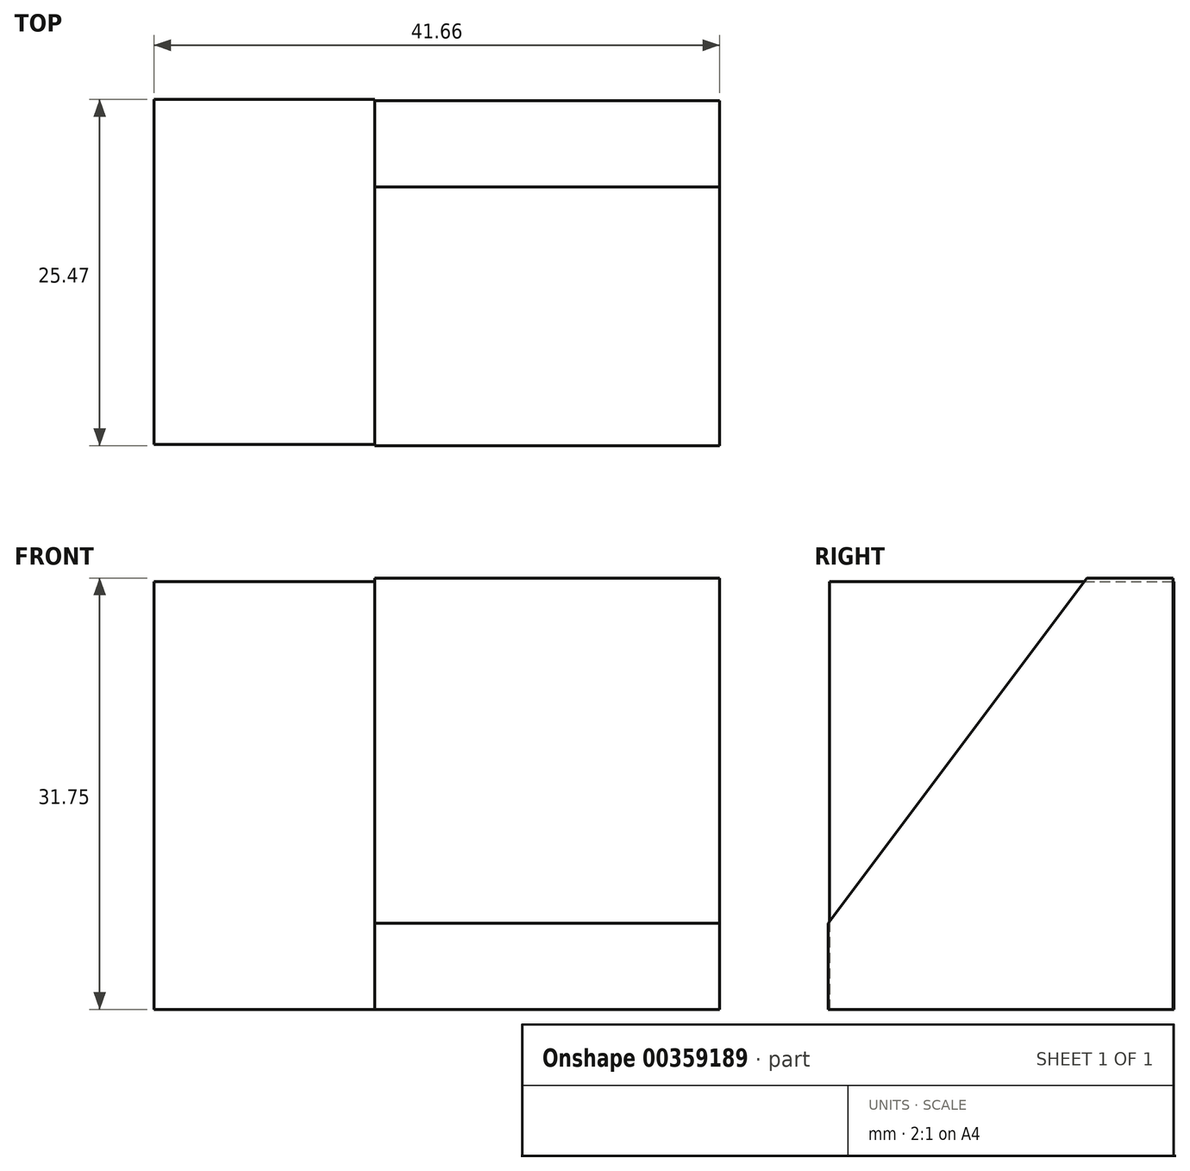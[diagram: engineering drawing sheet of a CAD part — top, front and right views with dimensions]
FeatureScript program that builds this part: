
annotation { "Feature Type Name" : "Feature", "Feature Type Description" : "" }
export const myFeature = defineFeature(function(context is Context, id is Id, definition is map)
    precondition{}
    {
        {
            var Q0;
            Q0=qCreatedBy(makeId("Right.planeOp"),FACE);
            var sketch = newSketch(context, id + "F0", { "sketchPlane" : qUnion([Q0])});
            skLineSegment(sketch, "E0", {"start": v(0, 31.75) * mm, "end": v(6.35, 31.75) * mm});
            skLineSegment(sketch, "E1", {"start": v(6.35, 31.75) * mm, "end": v(6.35, 0) * mm});
            skLineSegment(sketch, "E2", {"start": v(6.35, 0) * mm, "end": v(-19.05, 0) * mm});
            skLineSegment(sketch, "E3", {"start": v(-19.05, 0) * mm, "end": v(-19.05, 6.35) * mm});
            skLineSegment(sketch, "E4", {"start": v(-19.05, 6.35) * mm, "end": v(0, 31.75) * mm});
            skSolve(sketch);
        }
        {
            var Q0;
            Q0 = qSketchRegion(id + "F0", true);
            var Q1;
            Q1=makeQuery(id+"F0.imprint","IMPRINT",FACE,{"disambiguationData":[TD([[makeQuery(id+"F0.imprint","IMPRINT",EDGE,{"derivedFrom":sQuery(id+"F0.wireOp",EDGE,"E0")}),-1.0]])]});
            extrude(context, id + "F1", {"entities" : qUnion([Q0, Q1]), "depth" : 25.4 * mm});
        }
        {
            var Q0;
            Q0=qCreatedBy(makeId("Top.planeOp"),FACE);
            var sketch = newSketch(context, id + "F2", { "sketchPlane" : qUnion([Q0])});
            skLineSegment(sketch, "E5", {"start": v(0, 6.42) * mm, "end": v(-16.26, 6.42) * mm});
            skLineSegment(sketch, "E6", {"start": v(0, -18.97) * mm, "end": v(0, 6.42) * mm});
            skLineSegment(sketch, "E7", {"start": v(0, -18.97) * mm, "end": v(-16.26, -18.97) * mm});
            skLineSegment(sketch, "E8", {"start": v(-16.26, -18.97) * mm, "end": v(-16.26, 6.42) * mm});
            skSolve(sketch);
        }
        {
            var Q0;
            Q0 = qSketchRegion(id + "F2", true);
            extrude(context, id + "F3", {"entities" : qUnion([Q0]), "operationType" : NewBodyOperationType.ADD, "depth" : 31.5 * mm});
        }
    });
